AUTODESK INVENTOR PART (.ipt)
format: ipt  version: 2019 (Build 230136000, 136)  size: 229,888 bytes
history: native  units: mm (DEFAULTED — no unit token found)
features: extrude x1, fillet x1, sketch x1
ambient origin geometry x8: Origin, YZ Plane, XZ Plane, XY Plane, X Axis, Y Axis, Z Axis, Center Point
bodies: Body1 (feature_tree)
feature tree (3):
  extrude  "Extrusion2"  Depth=6.5mm
  fillet  "Fillet2"  Radius=8.0mm
  sketch  "Sketch1"  dims[d2=5.5mm d3=6.5mm d4=8.0mm d5=13.5mm d9=1.75mm d10=4.5mm d11=4.5mm d12=1.75mm d13=10.0mm d14=0.0mm d15=0.5mm]
